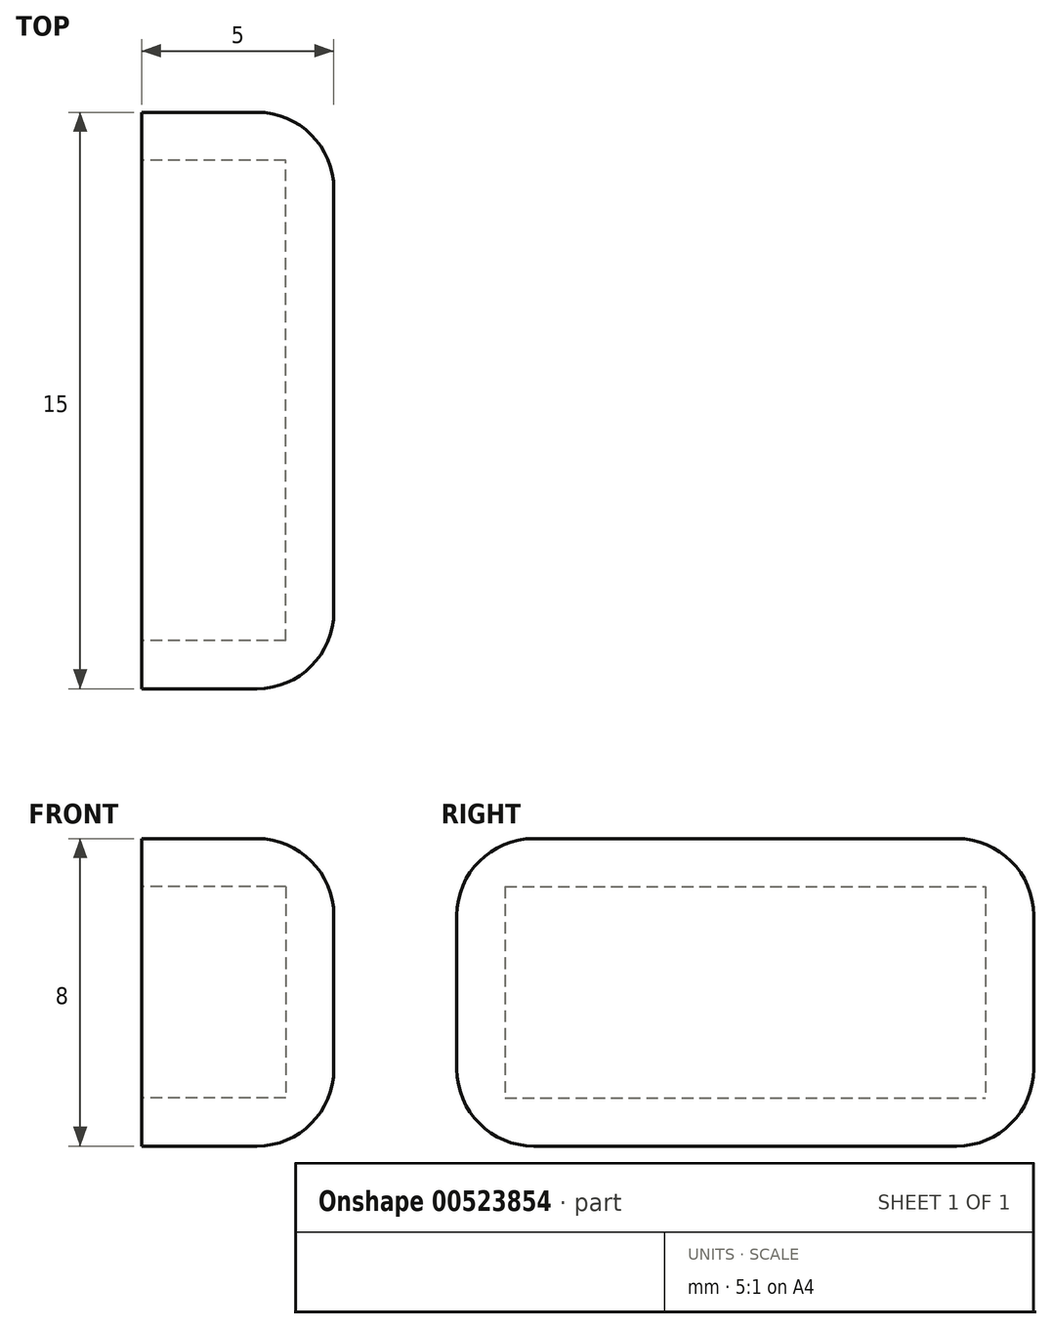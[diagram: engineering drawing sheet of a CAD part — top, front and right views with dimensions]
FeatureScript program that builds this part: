
annotation { "Feature Type Name" : "Feature", "Feature Type Description" : "" }
export const myFeature = defineFeature(function(context is Context, id is Id, definition is map)
    precondition{}
    {
        {
            var Q0;
            Q0=qCreatedBy(makeId("Right.planeOp"),FACE);
            var sketch = newSketch(context, id + "F0", { "sketchPlane" : qUnion([Q0])});
            skLineSegment(sketch, "E0.bottom", {"start": v(-7.5, 4) * mm, "end": v(7.5, 4) * mm});
            skLineSegment(sketch, "E0.top", {"start": v(-7.5, -4) * mm, "end": v(7.5, -4) * mm});
            skLineSegment(sketch, "E0.left", {"start": v(-7.5, 4) * mm, "end": v(-7.5, -4) * mm});
            skLineSegment(sketch, "E0.right", {"start": v(7.5, 4) * mm, "end": v(7.5, -4) * mm});
            skPoint(sketch, "E0.middle", {"position": v(0, 0) * mm});
            skSolve(sketch);
        }
        {
            var Q0;
            Q0=makeQuery(id+"F0.imprint","IMPRINT",FACE,{"disambiguationData":[TD([[makeQuery(id+"F0.imprint","IMPRINT",EDGE,{"derivedFrom":sQuery(id+"F0.wireOp",EDGE,"E0.bottom")}),-1.0]])]});
            extrude(context, id + "F1", {"entities" : qUnion([Q0]), "endBound" : BoundingType.SYMMETRIC, "depth" : 5 * mm, "offsetDistance" : 25 * mm});
        }
        {
            var Q0;
            Q0=makeQuery(id+"F1.opExtrude","CAP_FACE",FACE,{"disambiguationData":[OSD([sQuery(id+"F0.wireOp",EDGE,"E0.bottom"),sQuery(id+"F0.wireOp",EDGE,"E0.top"),sQuery(id+"F0.wireOp",EDGE,"E0.left"),sQuery(id+"F0.wireOp",EDGE,"E0.right")])],"isStart":true});
            var Q1;
            Q1=makeQuery(id+"FFoJCX8bP0vpMuj_1.opExtrude","SWEPT_FACE",FACE,{"disambiguationData":[OSD([sQuery(id+"FLzxutrhiEe1g9o_1.wireOp",EDGE,"RbAp52gx-LZsr-CybZ-8cQ9-zJUY45Q4m9PS.right")])]});
            shell(context, id + "F2", {"entities" : qUnion([Q0, Q1]), "thickness" : 1.25 * mm});
        }
        {
            var Q0;
            Q0=makeQuery(id+"F1.opExtrude","CAP_FACE",FACE,{"disambiguationData":[OSD([sQuery(id+"F0.wireOp",EDGE,"E0.bottom"),sQuery(id+"F0.wireOp",EDGE,"E0.top"),sQuery(id+"F0.wireOp",EDGE,"E0.left"),sQuery(id+"F0.wireOp",EDGE,"E0.right")])],"isStart":false});
            var Q1;
            Q1=makeQuery(id+"F1.opExtrude","SWEPT_EDGE",EDGE,{"disambiguationData":[OSD([sQuery(id+"F0.wireOp",EDGE,"E0.bottom"),sQuery(id+"F0.wireOp",EDGE,"E0.left")])]});
            var Q2;
            Q2=makeQuery(id+"F1.opExtrude","SWEPT_EDGE",EDGE,{"disambiguationData":[OSD([sQuery(id+"F0.wireOp",EDGE,"E0.bottom"),sQuery(id+"F0.wireOp",EDGE,"E0.right")])]});
            var Q3;
            Q3=makeQuery(id+"F1.opExtrude","SWEPT_EDGE",EDGE,{"disambiguationData":[OSD([sQuery(id+"F0.wireOp",EDGE,"E0.top"),sQuery(id+"F0.wireOp",EDGE,"E0.right")])]});
            var Q4;
            Q4=makeQuery(id+"F1.opExtrude","SWEPT_EDGE",EDGE,{"disambiguationData":[OSD([sQuery(id+"F0.wireOp",EDGE,"E0.top"),sQuery(id+"F0.wireOp",EDGE,"E0.left")])]});
            var Q5;
            Q5=makeQuery(id+"FFoJCX8bP0vpMuj_1.opExtrude","CAP_EDGE",EDGE,{"disambiguationData":[OSD([sQuery(id+"FLzxutrhiEe1g9o_1.wireOp",EDGE,"RbAp52gx-LZsr-CybZ-8cQ9-zJUY45Q4m9PS.left")])],"isStart":false});
            var Q6;
            Q6=makeQuery(id+"FFoJCX8bP0vpMuj_1.opExtrude","CAP_EDGE",EDGE,{"disambiguationData":[OSD([sQuery(id+"FLzxutrhiEe1g9o_1.wireOp",EDGE,"RbAp52gx-LZsr-CybZ-8cQ9-zJUY45Q4m9PS.top")])],"isStart":false});
            var Q7;
            Q7=makeQuery(id+"FFoJCX8bP0vpMuj_1.opExtrude","CAP_EDGE",EDGE,{"disambiguationData":[OSD([sQuery(id+"FLzxutrhiEe1g9o_1.wireOp",EDGE,"RbAp52gx-LZsr-CybZ-8cQ9-zJUY45Q4m9PS.bottom")])],"isStart":false});
            fillet(context, id + "F3", {"entities" : qUnion([Q0, Q1, Q2, Q3, Q4, Q5, Q6, Q7]), "radius" : 2 * mm, "tangentPropagation" : true, "allowEdgeOverflow" : false});
        }
    });
